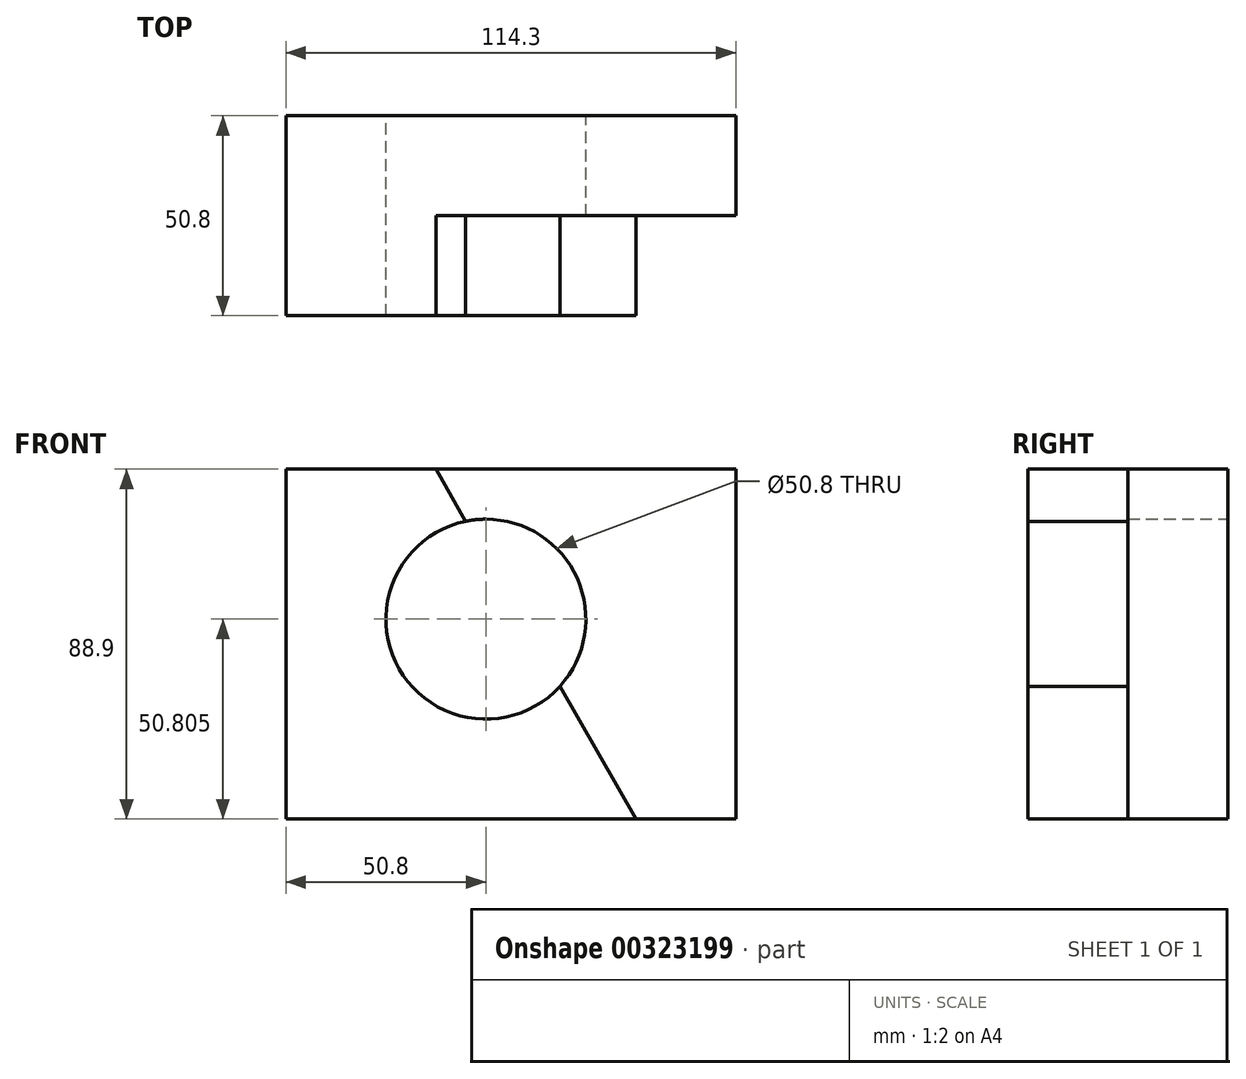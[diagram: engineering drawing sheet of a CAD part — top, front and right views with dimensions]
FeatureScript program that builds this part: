
annotation { "Feature Type Name" : "Feature", "Feature Type Description" : "" }
export const myFeature = defineFeature(function(context is Context, id is Id, definition is map)
    precondition{}
    {
        {
            var Q0;
            Q0=qCreatedBy(makeId("Front.planeOp"),FACE);
            var sketch = newSketch(context, id + "F0", { "sketchPlane" : qUnion([Q0])});
            skLineSegment(sketch, "E0.bottom", {"start": v(-38.52, 50.46) * mm, "end": v(75.78, 50.46) * mm});
            skLineSegment(sketch, "E0.top", {"start": v(-38.52, -38.44) * mm, "end": v(75.78, -38.44) * mm});
            skLineSegment(sketch, "E0.left", {"start": v(-38.52, 50.46) * mm, "end": v(-38.52, -38.44) * mm});
            skLineSegment(sketch, "E0.right", {"start": v(75.78, 50.46) * mm, "end": v(75.78, -38.44) * mm});
            skSolve(sketch);
        }
        {
            var Q0;
            Q0=makeQuery(id+"F0.imprint","IMPRINT",FACE,{"disambiguationData":[TD([[makeQuery(id+"F0.imprint","IMPRINT",EDGE,{"derivedFrom":sQuery(id+"F0.wireOp",EDGE,"E0.bottom")}),-1.0]])]});
            extrude(context, id + "F1", {"entities" : qUnion([Q0]), "depth" : 50.8 * mm});
        }
        {
            var Q0;
            Q0=makeQuery(id+"F1.opExtrude","CAP_FACE",FACE,{"disambiguationData":[OSD([sQuery(id+"F0.wireOp",EDGE,"E0.bottom"),sQuery(id+"F0.wireOp",EDGE,"E0.top"),sQuery(id+"F0.wireOp",EDGE,"E0.left"),sQuery(id+"F0.wireOp",EDGE,"E0.right")])],"isStart":false});
            var sketch = newSketch(context, id + "F2", { "sketchPlane" : qUnion([Q0])});
            skLineSegment(sketch, "E1", {"start": v(-38.52, 50.46) * mm, "end": v(-0.42, 50.46) * mm});
            skLineSegment(sketch, "E2", {"start": v(-0.42, 50.46) * mm, "end": v(50.38, -38.44) * mm});
            skLineSegment(sketch, "E3", {"start": v(50.38, -38.44) * mm, "end": v(-38.52, -38.44) * mm});
            skLineSegment(sketch, "E4", {"start": v(-38.52, -38.44) * mm, "end": v(-38.52, 50.46) * mm});
            skLineSegment(sketch, "E5", {"start": v(-0.42, 50.46) * mm, "end": v(75.78, 50.46) * mm});
            skLineSegment(sketch, "E6", {"start": v(75.78, 50.46) * mm, "end": v(75.78, -38.44) * mm});
            skLineSegment(sketch, "E7", {"start": v(75.78, -38.44) * mm, "end": v(50.38, -38.44) * mm});
            skSolve(sketch);
        }
        {
            var Q0;
            Q0=makeQuery(id+"F2.imprint","IMPRINT",FACE,{"disambiguationData":[TD([[makeQuery(id+"F2.imprint","IMPRINT",EDGE,{"derivedFrom":sQuery(id+"F2.wireOp",EDGE,"E2")}),1.0]])]});
            extrude(context, id + "F3", {"entities" : qUnion([Q0]), "operationType" : NewBodyOperationType.REMOVE, "oppositeDirection" : true, "depth" : 25.4 * mm});
        }
        {
            var Q0;
            Q0=makeQuery(id+"F1.opExtrude","CAP_FACE",FACE,{"disambiguationData":[OSD([sQuery(id+"F0.wireOp",EDGE,"E0.bottom"),sQuery(id+"F0.wireOp",EDGE,"E0.top"),sQuery(id+"F0.wireOp",EDGE,"E0.left"),sQuery(id+"F0.wireOp",EDGE,"E0.right")])],"isStart":true});
            var sketch = newSketch(context, id + "F4", { "sketchPlane" : qUnion([Q0])});
            skLineSegment(sketch, "E8", {"start": v(-75.78, 50.46) * mm, "end": v(-75.78, 12.36) * mm});
            skLineSegment(sketch, "E9", {"start": v(-75.78, 50.46) * mm, "end": v(-12.28, 50.46) * mm});
            skCircle(sketch, "E10", {"center": v(-12.28, 12.36) * mm, "radius": 25.4 * mm});
            skSolve(sketch);
        }
        {
            var Q0;
            Q0=makeQuery(id+"F4.imprint","IMPRINT",FACE,{"disambiguationData":[TD([[makeQuery(id+"F4.imprint","IMPRINT",EDGE,{"derivedFrom":sQuery(id+"F4.wireOp",EDGE,"E10")}),1.0]])]});
            extrude(context, id + "F5", {"entities" : qUnion([Q0]), "operationType" : NewBodyOperationType.REMOVE, "oppositeDirection" : true, "depth" : 50.8 * mm});
        }
    });
